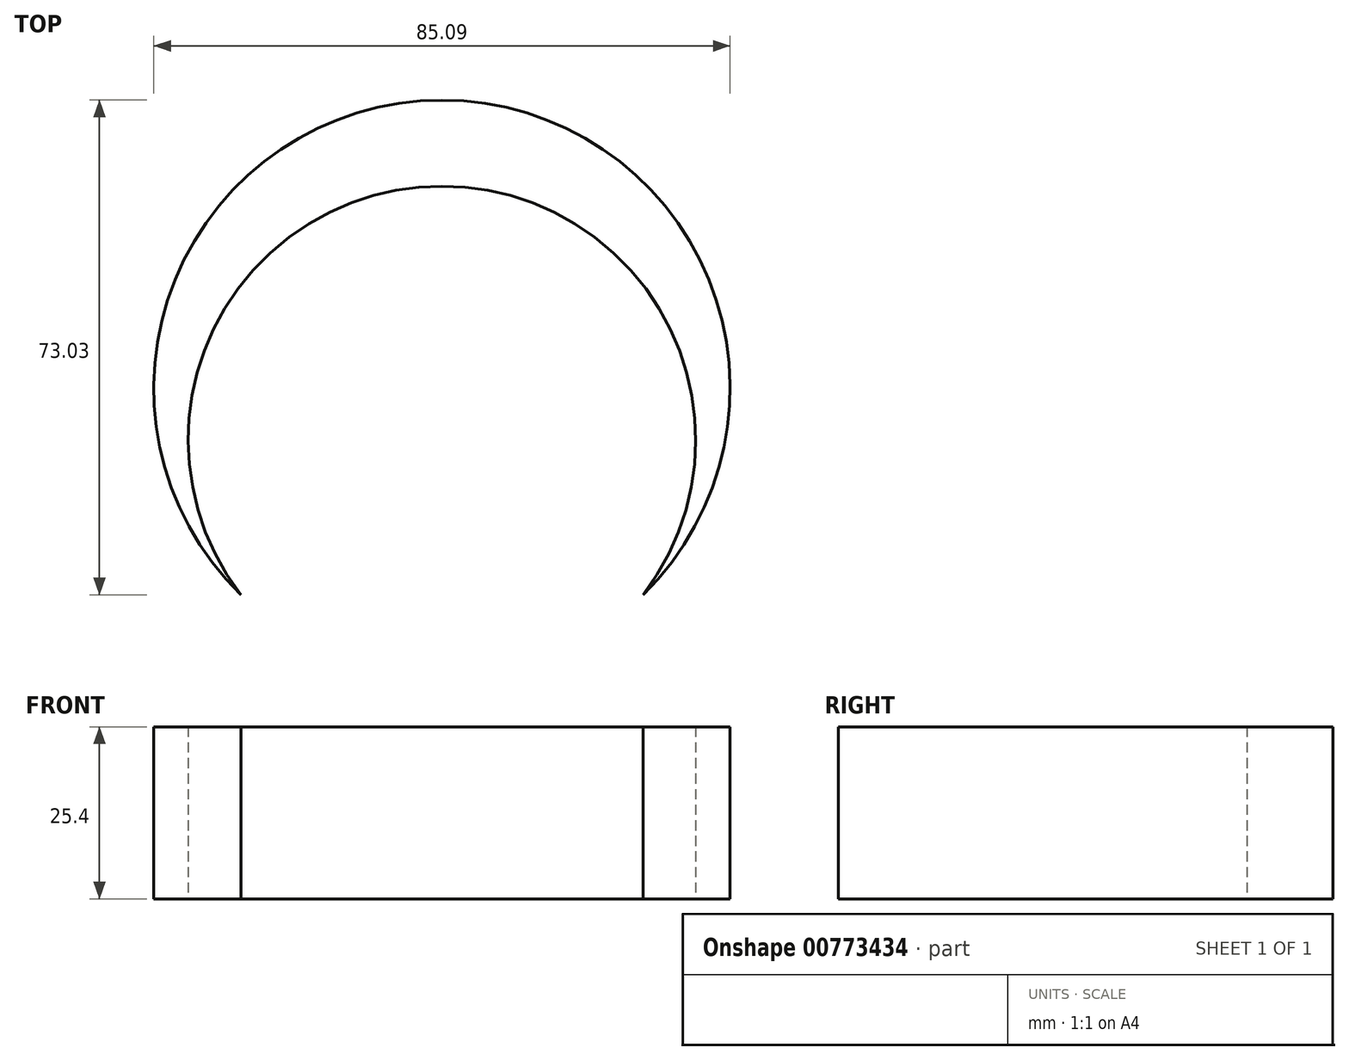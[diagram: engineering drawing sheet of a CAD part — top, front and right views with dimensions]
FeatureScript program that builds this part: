
annotation { "Feature Type Name" : "Feature", "Feature Type Description" : "" }
export const myFeature = defineFeature(function(context is Context, id is Id, definition is map)
    precondition{}
    {
        {
            var Q0;
            Q0=qCreatedBy(makeId("Top.planeOp"),FACE);
            var sketch = newSketch(context, id + "F0", { "sketchPlane" : qUnion([Q0])});
            skCircle(sketch, "E0", {"center": v(0, 0) * mm, "radius": 42.55 * mm});
            skCircle(sketch, "E1", {"center": v(0, -7.62) * mm, "radius": 37.47 * mm});
            skSolve(sketch);
        }
        {
            var Q0;
            {var subQ0=sQuery(id+"F0.wireOp",EDGE,"E1");var subQ1=sQuery(id+"F0.wireOp",EDGE,"E0");var subQ2=makeQuery(id+"F0.imprint","INTERSECT",VERTEX,{"disambiguationData":[OD(0.0)],"derivedFrom":[subQ1,subQ0]});Q0=makeQuery(id+"F0.imprint","IMPRINT",FACE,{"disambiguationData":[TD([[makeQuery(id+"F0.imprint","IMPRINT",EDGE,{"disambiguationData":[TD([[subQ2,1.0]])],"derivedFrom":subQ1}),1.0]])]});}
            extrude(context, id + "F1", {"entities" : qUnion([Q0]), "depth" : 25.4 * mm});
        }
    });
